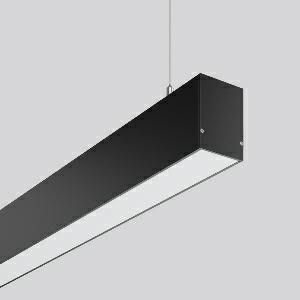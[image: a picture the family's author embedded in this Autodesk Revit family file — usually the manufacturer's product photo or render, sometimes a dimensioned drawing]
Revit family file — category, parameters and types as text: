
# Revit family: less_is_more_50_312320_003_1_3cdf
name_source: partatom
category: Lighting Fixtures
units: mm (PartAtom-declared; Revit-internal decimal feet)

## family parameters
Cut with Voids When Loaded = No
Host = Face
Light Source = No
Part Type = Normal
Room Calculation Point = No
Round Connector Dimension = Use Diameter
Shared = No

## types (1)
- LESS IS MORE 50 (1 x LED Modul 840, 7250 lm, 4000)
    Apparent Load = 59 VA
    CIE Flux Codes = 49 80 96 63 100
    Color Rendering = 80
    Color Temperature = 4000
    Default Elevation = 1800 mm
    Description = Series: LESS IS MORE 50
Linear pendant luminaire for aesthetically sophisticated lighting. Housing: extruded aluminium profile, powder-coated. End cap aluminium powder-coated. Canopy made of aluminium, powder-coated. Diffuser made of non-yellowing plastic (PMMA), opal. Direct 65%, indirect 35% light emission. Suitable for pendant. 2-point steel cable suspension freely positionable and infinitely height-adjustable. Special lengths available on request. LED unit with integrated converter interchangeable and removable. Suitable for through-wiring. With sensors or as a safety luminaire on request. 
Colour: deep black, matt (RAL 9005)
Length: 1687 mm
Width: 57 mm
Height: 75 mm
Suspension length: 2000 mm
Lamp: LED
Socket: without socket
Colour temperature: 4000K
Colour rendering index (CRI): 80
Light source: LED
Socket lamp2: Without base
Colour temperature: 4000K
System power: 59 W
Rated luminous flux: 7250 lm
Luminous efficiency: 123 lm/W
Control gear: Regulated power supply
Control gear: Regulated power supply
Protection class: I
Type of protection: IP 20
    Height = 75 mm
    Lamp = 1 x LED Modul 840
    Lamp Light Flux = 7250 lm
    Lamp count = 1
    Length = 1687 mm
    Lifetime = 50000 h
    Luminous efficacy = 123 lm/W
    Manufacturer = RZB
    ModVariant = No
    Model = 312320.003.1
    Mounting Place = Ceiling
    Mounting Type = Pendant
    Number of Poles = 1
    OnlyDefault = Yes
    Power Factor = 1
    Product Name = LESS IS MORE 50
    Product group = Pendant LED linear luminaires
    ProductGroupID = 907
    Protection Class = Protection class I
    Protection Degree = IP 20
    RLX_Detail_Level = 1
    RLX_Emergency_Light_Flux = 0 lm
    RLX_Emergency_Type = 0
    RLX_Emergency_Type_DB = No
    RlxData = <blob elided: 39929 chars, md5=576287cd>
    Socket = socket
    Standby Power = 0 W
    System Light Flux = 7250 lm
    System Power = 59 W
    Type Comments = Product without accessories
    Type Image = 312318.003.jpg
    URL = http://relux.com
    VarID = ---
    Voltage = 230 V
    Voltage Range = 220-240 V
    Weight = 0.00 kg
    Width = 57 mm

## geometry (parser evidence)
native form markers: Blend x4, Sweep x13
no freeform markers — native parametric forms only
